# Revit family: LEGRAND_PRISES_NON_VERROUILLEES_ENCASTREES_IP44_400_SYMBOLE
name_source: partatom
category: Annotations génériques
revit_build: Autodesk Revit 2018 (Build: 20170223_1515(x64)
units: mm (PartAtom-declared; Revit-internal decimal feet)

## family parameters
Conserve la lisibilité du texte = Non
Partagée = Non
Rotation avec le composant = Non

## types (19) — shared parameters
Prises verrouillées = Non
diamètre symbole = 10 mm  [stored 0.0328084 ft]
rayon pole = 1 mm  [stored 0.00328084 ft]
rayon symbole = 5 mm  [stored 0.0164042 ft]
rayon verrouillage = 0.8 mm  [stored 0.00262467 ft]

## per-type parameters (varying)
| type | 2P+T | 3P+T | 3P+T+N |
| Symbole réf.052218 | Oui | Non | Non |
| Symbole réf.052219 | Oui | Non | Non |
| Symbole réf.052220 | Non | Non | Oui |
| Symbole réf.052222 | Oui | Non | Non |
| Symbole réf.052223 | Oui | Non | Non |
| Symbole réf.052224 | Non | Non | Oui |
| Symbole réf.052232 | Oui | Non | Non |
| Symbole réf.052233 | Non | Oui | Non |
| Symbole réf.052234 | Oui | Non | Non |
| Symbole réf.052920 | Oui | Non | Non |
| Symbole réf.052918 | Oui | Non | Non |
| Symbole réf.052919 | Non | Oui | Non |
| Symbole réf.052932 | Oui | Non | Non |
| Symbole réf.052933 | Non | Oui | Non |
| Symbole réf.052934 | Oui | Non | Non |
| Symbole réf.053823 | Non | Oui | Non |
| Symbole réf.053824 | Non | Oui | Non |
| Symbole réf.053833 | Non | Oui | Non |
| Symbole réf.053834 | Non | Non | Oui |

note: [stored X ft] marks values corroborated as IEEE doubles in the binary element streams (Revit-internal decimal feet)
